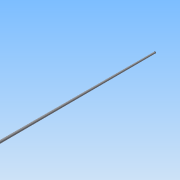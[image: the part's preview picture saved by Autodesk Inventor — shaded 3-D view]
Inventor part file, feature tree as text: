
AUTODESK INVENTOR PART (.ipt)
format: ipt  version: 2015 (Build 190159000, 159)  size: 63,488 bytes
history: native  units: mm
features: extrude x1, sketch x1
ambient origin geometry x8: Origin, YZ Plane, XZ Plane, XY Plane, X Axis, Y Axis, Z Axis, Center Point
bodies: Solid1 (feature_tree)
feature tree (2):
  extrude  "Extrusion1"  Depth=430.0mm TaperAngle=0.0deg
  sketch  "Sketch1"  dims[d0=5.0mm d1=430.0mm d2=0.0mm]
